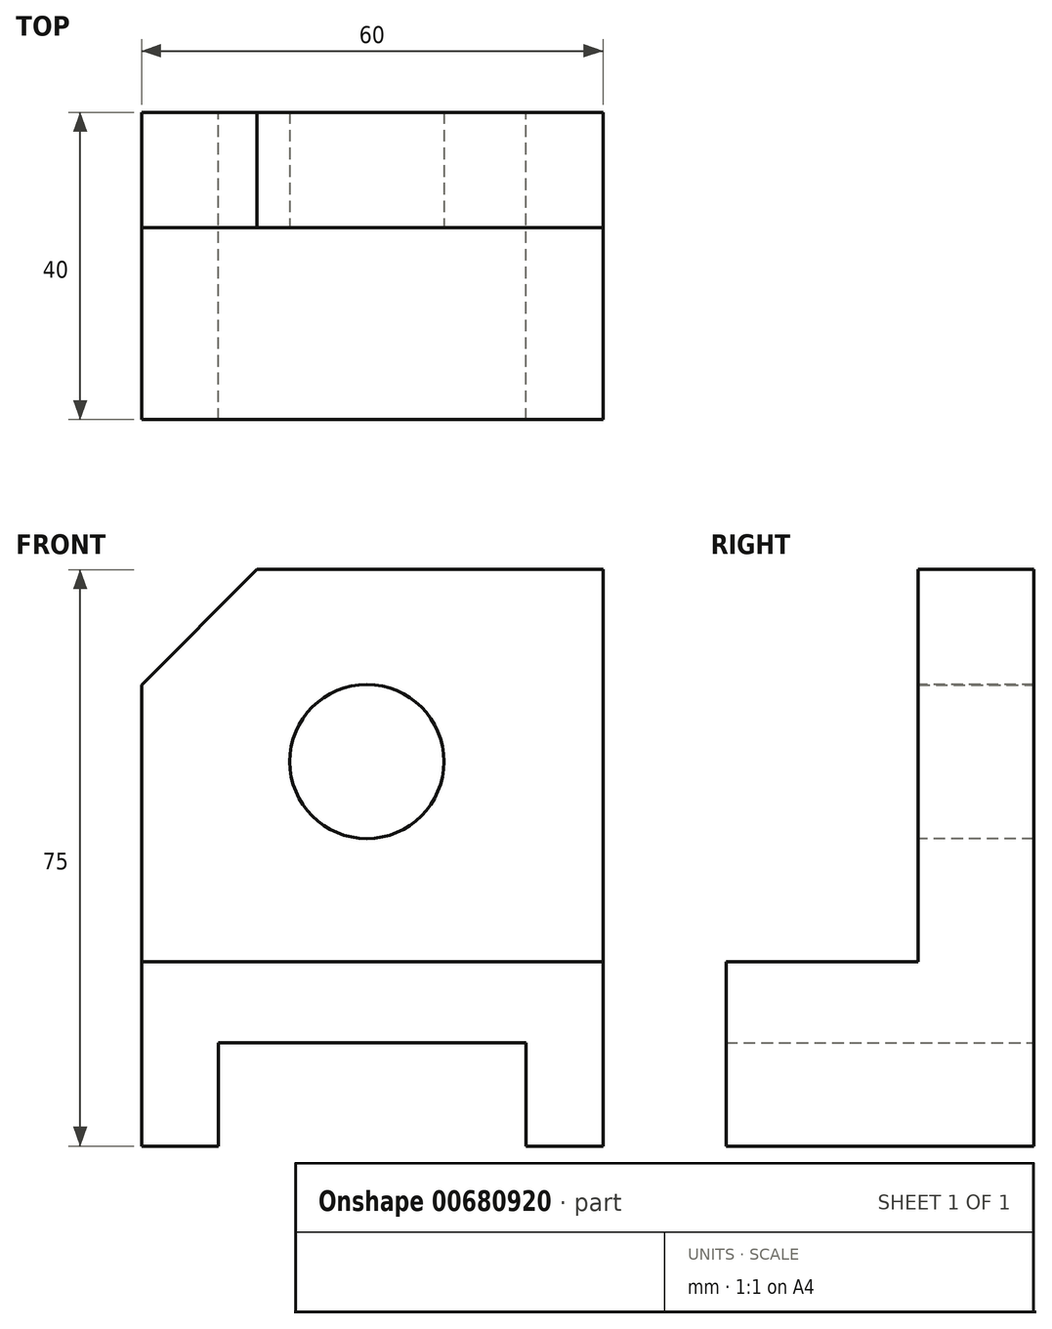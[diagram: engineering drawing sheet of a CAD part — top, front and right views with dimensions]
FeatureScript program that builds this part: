
annotation { "Feature Type Name" : "Feature", "Feature Type Description" : "" }
export const myFeature = defineFeature(function(context is Context, id is Id, definition is map)
    precondition{}
    {
        {
            var Q0;
            Q0=qCreatedBy(makeId("Front.planeOp"),FACE);
            var sketch = newSketch(context, id + "F0", { "sketchPlane" : qUnion([Q0])});
            skLineSegment(sketch, "E0", {"start": v(-36.75, 24.23) * mm, "end": v(-36.75, -35.77) * mm});
            skLineSegment(sketch, "E1", {"start": v(-36.75, -35.77) * mm, "end": v(-26.75, -35.77) * mm});
            skLineSegment(sketch, "E2", {"start": v(-26.75, -35.77) * mm, "end": v(-26.75, -22.33) * mm});
            skLineSegment(sketch, "E3", {"start": v(-26.75, -22.33) * mm, "end": v(13.25, -22.33) * mm});
            skLineSegment(sketch, "E4", {"start": v(13.25, -22.33) * mm, "end": v(13.25, -35.77) * mm});
            skLineSegment(sketch, "E5", {"start": v(13.25, -35.77) * mm, "end": v(23.25, -35.77) * mm});
            skLineSegment(sketch, "E6", {"start": v(23.25, -35.77) * mm, "end": v(23.25, 39.23) * mm});
            skLineSegment(sketch, "E7", {"start": v(23.25, 39.23) * mm, "end": v(-21.75, 39.23) * mm});
            skLineSegment(sketch, "E8", {"start": v(-21.75, 39.23) * mm, "end": v(-36.75, 24.23) * mm});
            skSolve(sketch);
        }
        {
            var Q0;
            Q0=makeQuery(id+"F0.imprint","IMPRINT",FACE,{"disambiguationData":[TD([[makeQuery(id+"F0.imprint","IMPRINT",EDGE,{"derivedFrom":sQuery(id+"F0.wireOp",EDGE,"E0")}),1.0]])]});
            extrude(context, id + "F1", {"entities" : qUnion([Q0]), "depth" : 15 * mm, "offsetDistance" : 25 * mm});
        }
        {
            var Q0;
            Q0=makeQuery(id+"F1.opExtrude","CAP_FACE",FACE,{"disambiguationData":[OSD([sQuery(id+"F0.wireOp",EDGE,"E0"),sQuery(id+"F0.wireOp",EDGE,"E1"),sQuery(id+"F0.wireOp",EDGE,"E2"),sQuery(id+"F0.wireOp",EDGE,"E3"),sQuery(id+"F0.wireOp",EDGE,"E4"),sQuery(id+"F0.wireOp",EDGE,"E5"),sQuery(id+"F0.wireOp",EDGE,"E6"),sQuery(id+"F0.wireOp",EDGE,"E7"),sQuery(id+"F0.wireOp",EDGE,"E8")])],"isStart":false});
            var sketch = newSketch(context, id + "F2", { "sketchPlane" : qUnion([Q0])});
            skLineSegment(sketch, "E9", {"start": v(-36.75, -11.81) * mm, "end": v(23.25, -11.81) * mm});
            skLineSegment(sketch, "E10", {"start": v(23.25, -11.81) * mm, "end": v(23.25, -35.77) * mm});
            skLineSegment(sketch, "E11", {"start": v(23.25, -35.77) * mm, "end": v(13.25, -35.77) * mm});
            skLineSegment(sketch, "E12", {"start": v(13.25, -35.77) * mm, "end": v(13.25, -22.33) * mm});
            skLineSegment(sketch, "E13", {"start": v(13.25, -22.33) * mm, "end": v(-26.75, -22.33) * mm});
            skLineSegment(sketch, "E14", {"start": v(-26.75, -22.33) * mm, "end": v(-26.75, -35.77) * mm});
            skLineSegment(sketch, "E15", {"start": v(-26.75, -35.77) * mm, "end": v(-36.75, -35.77) * mm});
            skLineSegment(sketch, "E16", {"start": v(-36.75, -35.77) * mm, "end": v(-36.75, -11.81) * mm});
            skSolve(sketch);
        }
        {
            var Q0;
            Q0=makeQuery(id+"F2.imprint","IMPRINT",FACE,{"disambiguationData":[TD([[makeQuery(id+"F2.imprint","IMPRINT",EDGE,{"derivedFrom":sQuery(id+"F2.wireOp",EDGE,"E9")}),-1.0]])]});
            extrude(context, id + "F3", {"entities" : qUnion([Q0]), "operationType" : NewBodyOperationType.ADD, "depth" : 25 * mm, "offsetDistance" : 25 * mm});
        }
        {
            var Q0;
            Q0=makeQuery(id+"F1.opExtrude","CAP_FACE",FACE,{"disambiguationData":[OSD([sQuery(id+"F0.wireOp",EDGE,"E0"),sQuery(id+"F0.wireOp",EDGE,"E1"),sQuery(id+"F0.wireOp",EDGE,"E2"),sQuery(id+"F0.wireOp",EDGE,"E3"),sQuery(id+"F0.wireOp",EDGE,"E4"),sQuery(id+"F0.wireOp",EDGE,"E5"),sQuery(id+"F0.wireOp",EDGE,"E6"),sQuery(id+"F0.wireOp",EDGE,"E7"),sQuery(id+"F0.wireOp",EDGE,"E8")])],"isStart":false});
            var sketch = newSketch(context, id + "F4", { "sketchPlane" : qUnion([Q0])});
            skCircle(sketch, "E17", {"center": v(-7.46, 14.25) * mm, "radius": 10.02 * mm});
            skSolve(sketch);
        }
        {
            var Q0;
            Q0=makeQuery(id+"F4.imprint","IMPRINT",FACE,{"disambiguationData":[TD([[makeQuery(id+"F4.imprint","IMPRINT",EDGE,{"derivedFrom":sQuery(id+"F4.wireOp",EDGE,"E17")}),1.0]])]});
            extrude(context, id + "F5", {"entities" : qUnion([Q0]), "operationType" : NewBodyOperationType.REMOVE, "oppositeDirection" : true, "depth" : 25 * mm, "offsetDistance" : 25 * mm});
        }
    });
